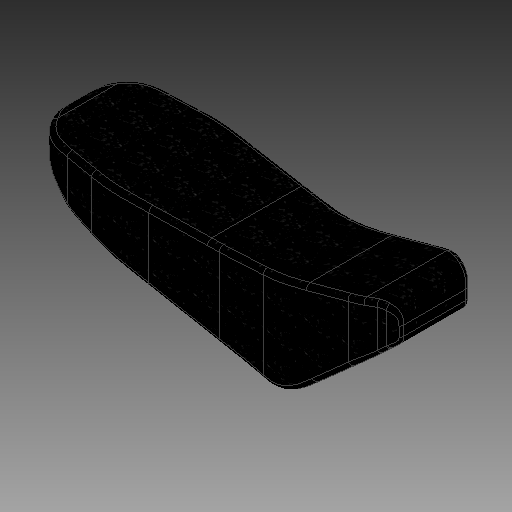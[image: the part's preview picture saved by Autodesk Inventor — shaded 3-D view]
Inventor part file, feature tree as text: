
AUTODESK INVENTOR PART (.ipt)
format: ipt  version: 2019.2 (Build 232265000, 265)  size: 5,956,096 bytes
history: native  units: mm
features: extrude x2, sketch x2, other x2, boolean_combine x1, fillet x1
ambient origin geometry x8: Origin, YZ Plane, XZ Plane, XY Plane, X Axis, Y Axis, Z Axis, Center Point
bodies: Solid1 (feature_tree), Solid3 (feature_tree)
feature tree (8):
  extrude  "Extrusion1"  Depth=180.0mm TaperAngle=0.0deg
  extrude  "Extrusion3"  Depth=6.0mm
  boolean_combine  "Combine2"
  fillet  "Fillet1"  [1 undecoded]
  sketch  "Sketch1"  dims[d3=490.0mm d83=180.0mm d84=0.0mm]
  other  "Image1"
  sketch  "Sketch3"  dims[d150=180.0mm d151=0.0mm d152=6.0mm]
  other  "Image2"
note: 1 required parameter value undecoded (feature->parameter linkage not recoverable at this tier; creation-order binding heuristic only, values carry confidence <= 0.55)
